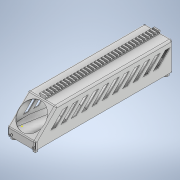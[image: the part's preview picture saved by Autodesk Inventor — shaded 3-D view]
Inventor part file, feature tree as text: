
AUTODESK INVENTOR PART (.ipt)
format: ipt  version: 2020 (Build 240168000, 168)  size: 735,744 bytes
history: native  units: mm
features: sketch x11, extrude x9, fillet x6, plane x4, revolve x1, shell x1, split x1, move_body x1, boolean_combine x1
ambient origin geometry x8: Origin, YZ Plane, XZ Plane, XY Plane, X Axis, Y Axis, Z Axis, Center Point
bodies: Solid1 (feature_tree), Solid4 (feature_tree), Solid5 (feature_tree)
feature tree (35):
  extrude  "Extrusion1"  Depth=80.0mm
  plane  "Work Plane1"
  revolve  "Revolution1"  [1 undecoded]
  shell  "Shell2"  Thickness=80.0mm
  plane  "Work Plane3"
  split  "Split2"
  move_body  "Move Body1"
  sketch  "Sketch6"  dims[d9=150.0mm d10=30.0mm]
  extrude  "Extrusion3"  Depth=30.0mm
  extrude  "Extrusion4"  TaperAngle=90.0deg  [1 undecoded]
  fillet  "Fillet1"  Radius=13.0mm
  fillet  "Fillet2"  [1 undecoded]
  fillet  "Fillet3"  Radius=2.0mm
  fillet  "Fillet4"  Radius=10.0mm
  extrude  "Extrusion6"  TaperAngle=0.0deg  [1 undecoded]
  extrude  "Extrusion8"  Depth=80.0mm TaperAngle=0.0deg
  boolean_combine  "Combine1"
  fillet  "Fillet5"  Radius=120.0mm
  extrude  "Extrusion9"  Depth=10.0mm
  fillet  "Fillet6"  Radius=10.0mm
  extrude  "Extrusion10"  Depth=10.0mm
  plane  "Work Plane4"
  sketch  "Sketch18"  dims[d39=78.0mm d40=0.0mm d41=78.0mm]
  plane  "Work Plane5"
  extrude  "Extrusion12"  Depth=78.0mm
  extrude  "Extrusion13"  Depth=100.0mm TaperAngle=0.0deg
  sketch  "Sketch2"  dims[d0=400.0mm d1=80.0mm]
  sketch  "Sketch5"  dims[d2=60.0mm d3=60.0mm d4=80.0mm d5=0.0mm]
  sketch  "Sketch8"  dims[d11=25.0mm d12=90.0deg d13=13.0mm d14=90.0deg d16=2.0mm]
  sketch  "Sketch9"  dims[d18=200.0mm d19=-200.0mm d20=0.0mm d21=10.0mm]
  sketch  "Sketch12"  dims[d24=10.0mm d25=0.0mm]
  sketch  "Sketch13"  dims[d26=10.0mm d27=0.0mm d28=80.0mm d29=0.0mm d30=120.0mm]
  sketch  "Sketch15"  dims[d33=15.0mm d34=15.0mm d35=10.0mm]
  sketch  "Sketch16"  dims[d36=10.0mm d38=27.0mm]
  sketch  "Sketch19"  dims[d42=76.0mm d45=3.0mm d46=0.0mm d47=5.0mm d48=10.0mm d49=5.0mm d50=5.0mm d51=10.0mm d52=20.0mm d54=62.0mm d55=20.0mm d57=382.0mm d60=5.0mm d61=5.0mm d62=10.0mm d63=0.0mm d64=5.0mm d65=50.0mm d66=45.0deg d67=15.0mm d68=135.0deg d69=50.0mm d70=45.0deg d71=180.0deg d72=30.0mm d73=10.0mm d74=105.0mm d76=30.0mm d77=10.0mm d79=10.0mm d81=80.0mm d82=0.0mm d93=90.0deg d94=15.67mm d95=21.2mm d96=45.0deg d97=135.0deg d98=9.32mm d99=45.0deg d100=135.0deg d101=90.0deg d102=100.0mm d103=0.0mm d104=4.75mm d105=5.25mm d106=350.0mm d108=10.0mm d109=10.0mm d111=10.0mm d113=100.0mm d114=0.0mm]
note: 4 required parameter values undecoded (feature->parameter linkage not recoverable at this tier; creation-order binding heuristic only, values carry confidence <= 0.55)